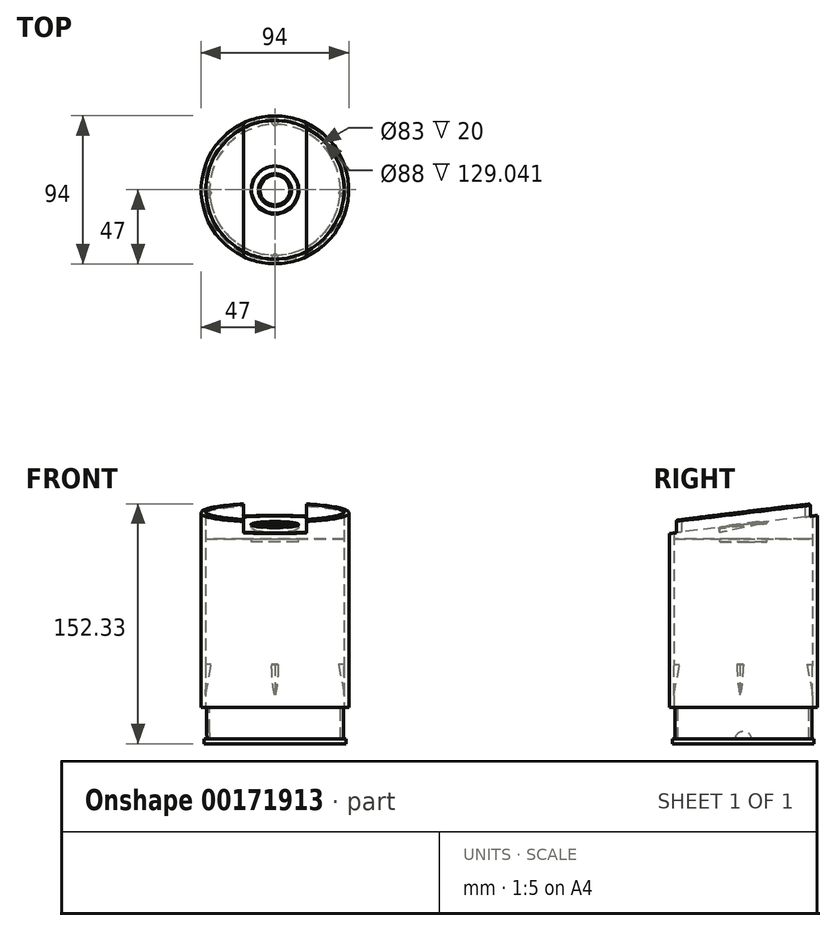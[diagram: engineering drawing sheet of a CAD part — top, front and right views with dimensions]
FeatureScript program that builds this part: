
annotation { "Feature Type Name" : "Feature", "Feature Type Description" : "" }
export const myFeature = defineFeature(function(context is Context, id is Id, definition is map)
    precondition{}
    {
        {
            var Q0;
            Q0=qCreatedBy(makeId("Top.planeOp"),FACE);
            var sketch = newSketch(context, id + "F0", { "sketchPlane" : qUnion([Q0])});
            skCircle(sketch, "E0", {"center": v(0, 0) * mm, "radius": 47 * mm});
            skCircle(sketch, "E1.0", {"center": v(0, 0) * mm, "radius": 44 * mm});
            skSolve(sketch);
        }
        {
            var Q0;
            Q0 = qSketchRegion(id + "F0", true);
            extrude(context, id + "F1", {"entities" : qUnion([Q0]), "depth" : 130 * mm});
        }
        {
            var Q0;
            Q0=qCreatedBy(makeId("Right.planeOp"),FACE);
            var sketch = newSketch(context, id + "F2", { "sketchPlane" : qUnion([Q0])});
            skLineSegment(sketch, "E2", {"start": v(-47, 118.46) * mm, "end": v(47, 130) * mm});
            skLineSegment(sketch, "E3", {"start": v(-47, 118.46) * mm, "end": v(-47, 130) * mm});
            skLineSegment(sketch, "E4", {"start": v(-47, 130) * mm, "end": v(47, 130) * mm});
            skSolve(sketch);
        }
        {
            var Q0;
            Q0 = qSketchRegion(id + "F2", true);
            extrude(context, id + "F3", {"entities" : qUnion([Q0]), "operationType" : NewBodyOperationType.REMOVE, "endBound" : BoundingType.SYMMETRIC, "oppositeDirection" : true, "depth" : 100 * mm});
        }
        {
            var Q0;
            Q0=makeQuery(id+"F3.boolean.opBoolean","INTERSECT",EDGE,{"derivedFrom":[makeQuery(id+"F1.opExtrude","SWEPT_FACE",FACE,{"disambiguationData":[OSD([sQuery(id+"F0.wireOp",EDGE,"E0")])]}),makeQuery(id+"F3.opExtrude","SWEPT_FACE",FACE,{"disambiguationData":[OSD([sQuery(id+"F2.wireOp",EDGE,"E2")])]})]});
            fillet(context, id + "F4", {"entities" : qUnion([Q0]), "radius" : 1 * mm, "tangentPropagation" : true, "allowEdgeOverflow" : false});
        }
        {
            var Q0;
            Q0=qCreatedBy(makeId("Top.planeOp"),FACE);
            cPlane(context, id + "F5", {"entities" : qUnion([Q0]), "cplaneType" : CPlaneType.OFFSET, "offset" : 130 * mm, "width" : 150 * mm, "height" : 150 * mm});
        }
        {
            var Q0;
            Q0=qCreatedBy(id+"F5.planeOp",FACE);
            var sketch = newSketch(context, id + "F6", { "sketchPlane" : qUnion([Q0])});
            skCircle(sketch, "E5", {"center": v(0, 0) * mm, "radius": 44 * mm});
            skSolve(sketch);
        }
        {
            var Q0;
            Q0 = qSketchRegion(id + "F6", true);
            extrude(context, id + "F7", {"entities" : qUnion([Q0]), "endBound" : BoundingType.SYMMETRIC, "depth" : 50 * mm});
        }
        {
            var Q0;
            Q0=qCreatedBy(makeId("Right.planeOp"),FACE);
            var sketch = newSketch(context, id + "F8", { "sketchPlane" : qUnion([Q0])});
            skLineSegment(sketch, "E6", {"start": v(-47, 130) * mm, "end": v(47, 130) * mm});
            skLineSegment(sketch, "E7", {"start": v(47, 130) * mm, "end": v(-47, 118.46) * mm});
            skLineSegment(sketch, "E8", {"start": v(-47, 130) * mm, "end": v(-47, 0) * mm});
            skLineSegment(sketch, "E9.top", {"start": v(-47, 200) * mm, "end": v(47, 200) * mm});
            skLineSegment(sketch, "E9.left", {"start": v(-47, 130) * mm, "end": v(-47, 200) * mm});
            skLineSegment(sketch, "E9.right", {"start": v(47, 130) * mm, "end": v(47, 200) * mm});
            skSolve(sketch);
        }
        {
            var Q0;
            Q0=makeQuery(id+"F8.imprint","IMPRINT",FACE,{"disambiguationData":[TD([[makeQuery(id+"F8.imprint","IMPRINT",EDGE,{"derivedFrom":sQuery(id+"F8.wireOp",EDGE,"E6")}),1.0]])]});
            var Q1;
            {var subQ0=sQuery(id+"F8.wireOp",EDGE,"E7");Q1=makeQuery(id+"F8.imprint","IMPRINT",FACE,{"disambiguationData":[TD([[makeQuery(id+"F8.imprint","IMPRINT",EDGE,{"derivedFrom":subQ0}),-1.0]])]});}
            extrude(context, id + "F9", {"entities" : qUnion([Q0, Q1]), "operationType" : NewBodyOperationType.REMOVE, "endBound" : BoundingType.SYMMETRIC, "oppositeDirection" : true, "depth" : 150 * mm});
        }
        {
            var Q0;
            Q0=makeQuery(id+"F9.boolean.opBoolean","INTERSECT",EDGE,{"derivedFrom":[makeQuery(id+"F7.opExtrude","SWEPT_FACE",FACE,{"disambiguationData":[OSD([sQuery(id+"F6.wireOp",EDGE,"E5")])]}),makeQuery(id+"F9.opExtrude","SWEPT_FACE",FACE,{"disambiguationData":[OSD([sQuery(id+"F8.wireOp",EDGE,"E7")])]})]});
            fillet(context, id + "F10", {"entities" : qUnion([Q0]), "radius" : 1 * mm, "tangentPropagation" : true, "allowEdgeOverflow" : false});
        }
        {
            var Q0;
            Q0=qCreatedBy(id+"F5.planeOp",FACE);
            var sketch = newSketch(context, id + "F11", { "sketchPlane" : qUnion([Q0])});
            skCircle(sketch, "E10", {"center": v(0, 0) * mm, "radius": 15 * mm});
            skSolve(sketch);
        }
        {
            var Q0;
            Q0 = qSketchRegion(id + "F11", true);
            extrude(context, id + "F12", {"entities" : qUnion([Q0]), "operationType" : NewBodyOperationType.REMOVE, "oppositeDirection" : true, "depth" : 50 * mm});
        }
        {
            var Q0;
            Q0=makeQuery(id+"F12.boolean.opBoolean","INTERSECT",EDGE,{"derivedFrom":[makeQuery(id+"F9.boolean.opBoolean","COPY",FACE,{"derivedFrom":makeQuery(id+"F9.opExtrude","SWEPT_FACE",FACE,{"disambiguationData":[OSD([sQuery(id+"F8.wireOp",EDGE,"E7")])]})}),makeQuery(id+"F12.opExtrude","SWEPT_FACE",FACE,{"disambiguationData":[OSD([sQuery(id+"F11.wireOp",EDGE,"E10")])]})]});
            fillet(context, id + "F13", {"entities" : qUnion([Q0]), "radius" : 10 * mm, "tangentPropagation" : true, "allowEdgeOverflow" : false});
        }
        {
            var Q0;
            Q0=qCreatedBy(id+"F5.planeOp",FACE);
            var sketch = newSketch(context, id + "F14", { "sketchPlane" : qUnion([Q0])});
            skCircle(sketch, "E11", {"center": v(0, 0) * mm, "radius": 15 * mm});
            skSolve(sketch);
        }
        {
            var Q0;
            Q0 = qSketchRegion(id + "F14", true);
            extrude(context, id + "F15", {"entities" : qUnion([Q0]), "oppositeDirection" : true, "depth" : 25 * mm});
        }
        {
            var Q0;
            Q0=qCreatedBy(makeId("Right.planeOp"),FACE);
            var sketch = newSketch(context, id + "F16", { "sketchPlane" : qUnion([Q0])});
            skLineSegment(sketch, "E12", {"start": v(-53, 142) * mm, "end": v(47, 142) * mm});
            skLineSegment(sketch, "E13", {"start": v(47, 142) * mm, "end": v(47, 122) * mm});
            skLineSegment(sketch, "E14", {"start": v(47, 122) * mm, "end": v(-53, 122) * mm});
            skLineSegment(sketch, "E15", {"start": v(-53, 122) * mm, "end": v(-53, 142) * mm});
            skLineSegment(sketch, "E16", {"start": v(47, 122) * mm, "end": v(-53, 109.72) * mm});
            skLineSegment(sketch, "E17", {"start": v(-53, 122) * mm, "end": v(-53, 109.72) * mm});
            skSolve(sketch);
        }
        {
            var Q0;
            Q0 = qSketchRegion(id + "F16", true);
            extrude(context, id + "F17", {"entities" : qUnion([Q0]), "operationType" : NewBodyOperationType.REMOVE, "endBound" : BoundingType.SYMMETRIC, "oppositeDirection" : true, "depth" : 40 * mm});
        }
        {
            var Q0;
            Q0=makeQuery(id+"F17.boolean.opBoolean","INTERSECT",EDGE,{"derivedFrom":[makeQuery(id+"F15.opExtrude","SWEPT_FACE",FACE,{"disambiguationData":[OSD([sQuery(id+"F14.wireOp",EDGE,"E11")])]}),makeQuery(id+"F17.opExtrude","SWEPT_FACE",FACE,{"disambiguationData":[OSD([sQuery(id+"F16.wireOp",EDGE,"E16")])]})]});
            fillet(context, id + "F18", {"entities" : qUnion([Q0]), "radius" : 1 * mm, "tangentPropagation" : true, "allowEdgeOverflow" : false});
        }
        {
            var Q0;
            Q0=makeQuery(id+"F17.boolean.opBoolean","COPY",FACE,{"derivedFrom":makeQuery(id+"F17.opExtrude","SWEPT_FACE",FACE,{"disambiguationData":[OSD([sQuery(id+"F16.wireOp",EDGE,"E16")])]})});
            var sketch = newSketch(context, id + "F19", { "sketchPlane" : qUnion([Q0])});
            skCircle(sketch, "E18", {"center": v(0, 14.04) * mm, "radius": 9.5 * mm});
            skCircle(sketch, "E19.0", {"center": v(0, 14.04) * mm, "radius": 10.5 * mm});
            skSolve(sketch);
        }
        {
            var Q0;
            Q0 = qSketchRegion(id + "F19", true);
            extrude(context, id + "F20", {"entities" : qUnion([Q0]), "operationType" : NewBodyOperationType.ADD, "depth" : 0.5 * mm});
        }
        {
            var Q0;
            Q0=makeQuery(id+"F20.opExtrude","CAP_EDGE",EDGE,{"disambiguationData":[OSD([sQuery(id+"F19.wireOp",EDGE,"E19.0")])],"isStart":false});
            var Q1;
            Q1=makeQuery(id+"F20.opExtrude","CAP_EDGE",EDGE,{"disambiguationData":[OSD([sQuery(id+"F19.wireOp",EDGE,"E18")])],"isStart":false});
            fillet(context, id + "F21", {"entities" : qUnion([Q0, Q1]), "radius" : 0.5 * mm, "tangentPropagation" : true, "allowEdgeOverflow" : false});
        }
        {
            var Q0;
            Q0=makeQuery(id+"F7.opExtrude","CAP_FACE",FACE,{"disambiguationData":[OSD([sQuery(id+"F6.wireOp",EDGE,"E5")])],"isStart":true});
            extrude(context, id + "F22", {"entities" : qUnion([Q0]), "operationType" : NewBodyOperationType.REMOVE, "oppositeDirection" : true, "depth" : 2 * mm});
        }
        {
            var Q0;
            Q0=makeQuery(id+"F22.boolean.opBoolean","COPY",FACE,{"derivedFrom":makeQuery(id+"F22.opExtrude","CAP_FACE",FACE,{"disambiguationData":[OSD([sQuery(id+"F6.wireOp",EDGE,"E5")])],"isStart":false})});
            var sketch = newSketch(context, id + "F23", { "sketchPlane" : qUnion([Q0])});
            skCircle(sketch, "E20", {"center": v(0, 0) * mm, "radius": 12 * mm});
            skCircle(sketch, "E21.0", {"center": v(0, 0) * mm, "radius": 17 * mm});
            skSolve(sketch);
        }
        {
            var Q0;
            Q0 = qSketchRegion(id + "F23", true);
            extrude(context, id + "F24", {"entities" : qUnion([Q0]), "operationType" : NewBodyOperationType.ADD, "oppositeDirection" : true, "depth" : 2 * mm});
        }
        {
            var Q0;
            Q0=qCreatedBy(makeId("Right.planeOp"),FACE);
            var sketch = newSketch(context, id + "F25", { "sketchPlane" : qUnion([Q0])});
            skLineSegment(sketch, "E22", {"start": v(-27.92, 81.21) * mm, "end": v(-46.7, 81.21) * mm});
            skLineSegment(sketch, "E23", {"start": v(-36.72, 90.4) * mm, "end": v(-51.73, 90.4) * mm});
            skLineSegment(sketch, "E24.bottom", {"start": v(0, 0) * mm, "end": v(-33.9, 0) * mm});
            skLineSegment(sketch, "E25", {"start": v(-45, 27.5) * mm, "end": v(-40, 27.5) * mm});
            skLineSegment(sketch, "E26", {"start": v(-45, 27.5) * mm, "end": v(-45, 0) * mm});
            skLineSegment(sketch, "E27", {"start": v(-45, 0) * mm, "end": v(-40, 27.5) * mm});
            skLineSegment(sketch, "E28.MirrorCS", {"start": v(45, 0) * mm, "end": v(40, 27.5) * mm});
            skLineSegment(sketch, "E29.MirrorCS", {"start": v(45, 27.5) * mm, "end": v(40, 27.5) * mm});
            skLineSegment(sketch, "E30.MirrorCS", {"start": v(45, 27.5) * mm, "end": v(45, 0) * mm});
            skSolve(sketch);
        }
        {
            var Q0;
            Q0 = qSketchRegion(id + "F25", true);
            extrude(context, id + "F26", {"entities" : qUnion([Q0]), "operationType" : NewBodyOperationType.ADD, "endBound" : BoundingType.SYMMETRIC, "depth" : 4 * mm});
        }
        {
            var Q0;
            Q0=qCreatedBy(makeId("Front.planeOp"),FACE);
            var sketch = newSketch(context, id + "F27", { "sketchPlane" : qUnion([Q0])});
            skLineSegment(sketch, "E31", {"start": v(-45, 27.5) * mm, "end": v(-45, 0) * mm});
            skLineSegment(sketch, "E32", {"start": v(-45, 0) * mm, "end": v(-40, 27.5) * mm});
            skLineSegment(sketch, "E33", {"start": v(-40, 27.5) * mm, "end": v(-45, 27.5) * mm});
            skLineSegment(sketch, "E34.MirrorCS", {"start": v(45, 0) * mm, "end": v(40, 27.5) * mm});
            skLineSegment(sketch, "E35.MirrorCS", {"start": v(40, 27.5) * mm, "end": v(45, 27.5) * mm});
            skLineSegment(sketch, "E36.MirrorCS", {"start": v(45, 27.5) * mm, "end": v(45, 0) * mm});
            skSolve(sketch);
        }
        {
            var Q0;
            Q0 = qSketchRegion(id + "F27", true);
            extrude(context, id + "F28", {"entities" : qUnion([Q0]), "operationType" : NewBodyOperationType.ADD, "depth" : 4 * mm});
        }
        {
            var Q0;
            Q0=makeQuery(id+"F28.opExtrude","CAP_EDGE",EDGE,{"disambiguationData":[OSD([sQuery(id+"F27.wireOp",EDGE,"E32")])],"isStart":true});
            var Q1;
            Q1=makeQuery(id+"F28.opExtrude","CAP_EDGE",EDGE,{"disambiguationData":[OSD([sQuery(id+"F27.wireOp",EDGE,"E32")])],"isStart":false});
            var Q2;
            Q2=makeQuery(id+"F26.opExtrude","CAP_EDGE",EDGE,{"disambiguationData":[OSD([sQuery(id+"F25.wireOp",EDGE,"E27")])],"isStart":true});
            var Q3;
            Q3=makeQuery(id+"F26.opExtrude","CAP_EDGE",EDGE,{"disambiguationData":[OSD([sQuery(id+"F25.wireOp",EDGE,"E27")])],"isStart":false});
            var Q4;
            Q4=makeQuery(id+"F28.opExtrude","CAP_EDGE",EDGE,{"disambiguationData":[OSD([sQuery(id+"F27.wireOp",EDGE,"E34.MirrorCS")])],"isStart":true});
            var Q5;
            Q5=makeQuery(id+"F28.opExtrude","CAP_EDGE",EDGE,{"disambiguationData":[OSD([sQuery(id+"F27.wireOp",EDGE,"E34.MirrorCS")])],"isStart":false});
            var Q6;
            Q6=makeQuery(id+"F26.opExtrude","CAP_EDGE",EDGE,{"disambiguationData":[OSD([sQuery(id+"F25.wireOp",EDGE,"E28.MirrorCS")])],"isStart":true});
            var Q7;
            Q7=makeQuery(id+"F26.opExtrude","CAP_EDGE",EDGE,{"disambiguationData":[OSD([sQuery(id+"F25.wireOp",EDGE,"E28.MirrorCS")])],"isStart":false});
            fillet(context, id + "F29", {"entities" : qUnion([Q0, Q1, Q2, Q3, Q4, Q5, Q6, Q7]), "radius" : 3.7 * mm, "tangentPropagation" : true, "allowEdgeOverflow" : false});
        }
        {
            var Q0;
            Q0=qCreatedBy(makeId("Top.planeOp"),FACE);
            var sketch = newSketch(context, id + "F30", { "sketchPlane" : qUnion([Q0])});
            skCircle(sketch, "E37", {"center": v(0, 0) * mm, "radius": 43.5 * mm});
            skCircle(sketch, "E38.0", {"center": v(0, 0) * mm, "radius": 41.5 * mm});
            skSolve(sketch);
        }
        {
            var Q0;
            Q0 = qSketchRegion(id + "F30", true);
            extrude(context, id + "F31", {"entities" : qUnion([Q0]), "oppositeDirection" : true, "depth" : 20 * mm});
        }
        {
            var Q0;
            Q0=qCreatedBy(makeId("Top.planeOp"),FACE);
            cPlane(context, id + "F32", {"entities" : qUnion([Q0]), "cplaneType" : CPlaneType.OFFSET, "offset" : 20 * mm, "oppositeDirection" : true, "width" : 150 * mm, "height" : 150 * mm});
        }
        {
            var Q0;
            Q0=qCreatedBy(id+"F32.planeOp",FACE);
            var sketch = newSketch(context, id + "F33", { "sketchPlane" : qUnion([Q0])});
            skCircle(sketch, "E39", {"center": v(0, 0) * mm, "radius": 45 * mm});
            skSolve(sketch);
        }
        {
            var Q0;
            Q0 = qSketchRegion(id + "F33", true);
            extrude(context, id + "F34", {"entities" : qUnion([Q0]), "operationType" : NewBodyOperationType.ADD, "oppositeDirection" : true, "depth" : 3 * mm});
        }
        {
            var Q0;
            Q0=qCreatedBy(makeId("Right.planeOp"),FACE);
            var sketch = newSketch(context, id + "F35", { "sketchPlane" : qUnion([Q0])});
            skArc(sketch, "E40", {"start": v(5, -20) * mm, "mid": v(0, -15) * mm, "end": v(-5, -20) * mm});
            skLineSegment(sketch, "E41", {"start": v(0, -20) * mm, "end": v(-7.1, -20) * mm});
            skLineSegment(sketch, "E42", {"start": v(-5, -20) * mm, "end": v(5, -20) * mm});
            skSolve(sketch);
        }
        {
            var Q0;
            Q0 = qSketchRegion(id + "F35", true);
            extrude(context, id + "F36", {"entities" : qUnion([Q0]), "operationType" : NewBodyOperationType.REMOVE, "oppositeDirection" : true, "depth" : 79.4 * mm});
        }
    });
